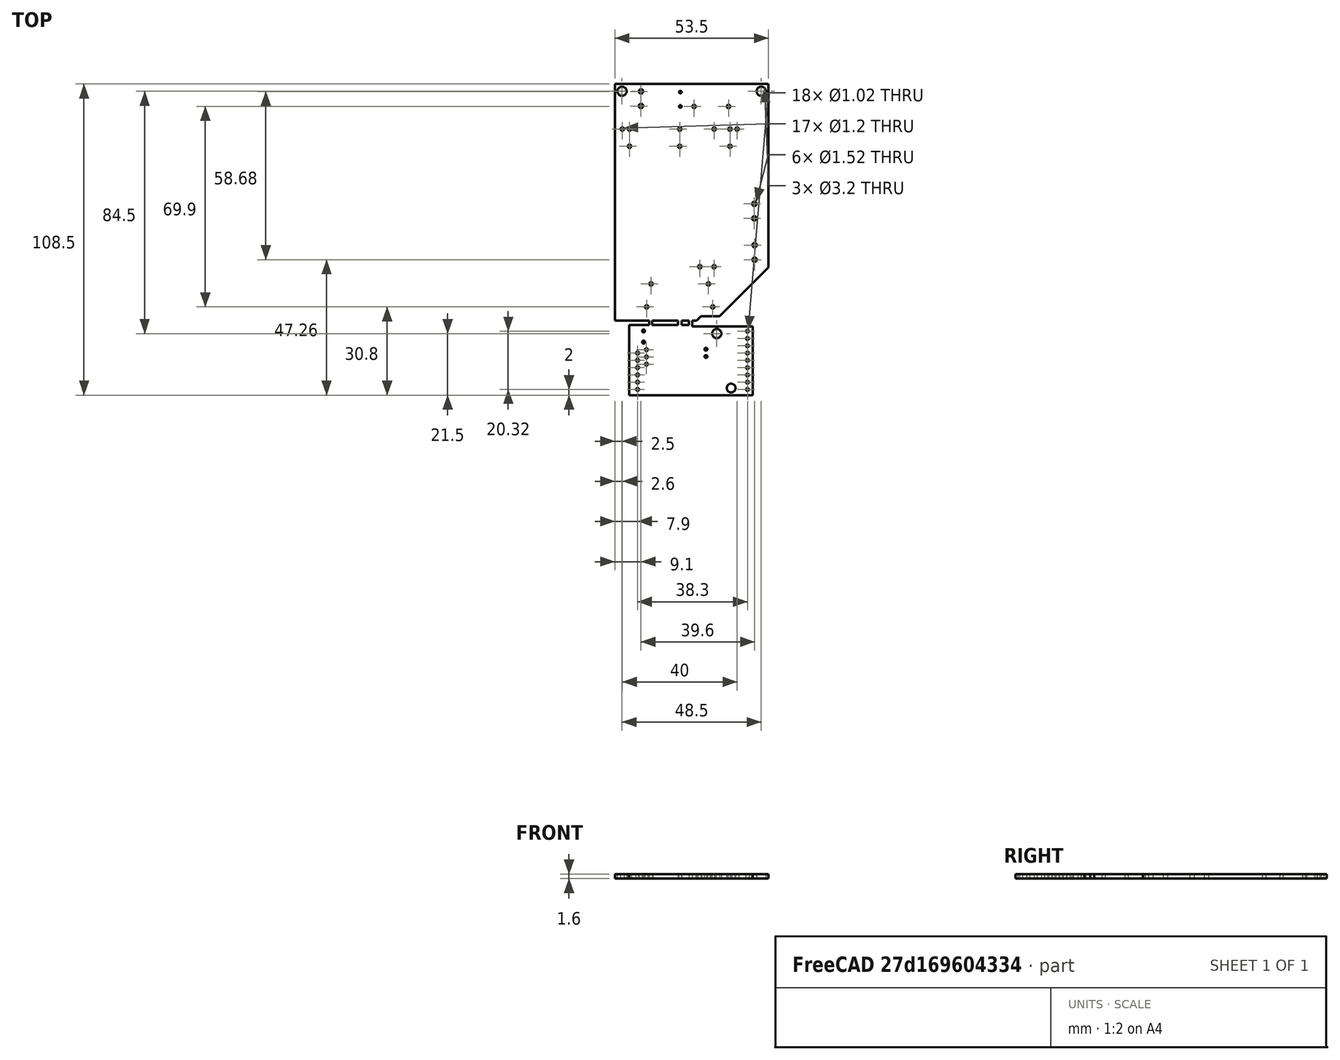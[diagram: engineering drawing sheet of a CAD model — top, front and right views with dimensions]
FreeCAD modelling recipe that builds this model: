
FCSTD DOCUMENT  (FreeCAD 0.16R)
Label: button1
License: All rights reserved
LicenseURL: http://en.wikipedia.org/wiki/All_rights_reserved
objects: App::DocumentObjectGroup×2, Part::Feature×1, Sketcher::SketchObject×1
note: 2 computed .brp shape members not serialized (recipe doc carries the construction recipe); baked Part::Feature solids carry a one-line shape summary decoded from their .brp

FEATURE [Part::Feature] Pcb
  Placement = pos=(-71.75,-78.75,0) rot=(0,0,1;0rad)
  shape: bbox 53.51 x 108.5 x 1.61 mm, 79 faces (baked)
FEATURE [Sketcher::SketchObject] PCB_Sketch
  sketch-geometry (26):
    g0: LineSegment StartX=0.25 StartY=-30.25 StartZ=0 EndX=0.75 EndY=-30.25 EndZ=0
    g1: LineSegment StartX=0.75 StartY=-28.25 StartZ=0 EndX=0.25 EndY=-28.25 EndZ=0
    g2: LineSegment StartX=0.25 StartY=-28.25 StartZ=0 EndX=0.25 EndY=-30.25 EndZ=0
    g3: LineSegment StartX=-21.75 StartY=-29.75 StartZ=0 EndX=-21.75 EndY=-30.25 EndZ=0
    g4: LineSegment StartX=-14.75 StartY=-29.75 StartZ=0 EndX=-21.75 EndY=-29.75 EndZ=0
    g5: LineSegment StartX=-14.75 StartY=-28.25 StartZ=0 EndX=-14.75 EndY=-29.75 EndZ=0
    g6: LineSegment StartX=-13.75 StartY=-29.75 StartZ=0 EndX=-13.75 EndY=-28.25 EndZ=0
    g7: LineSegment StartX=-4.75 StartY=-29.75 StartZ=0 EndX=-13.75 EndY=-29.75 EndZ=0
    g8: LineSegment StartX=-4.75 StartY=-29.75 StartZ=0 EndX=-4.75 EndY=-28.25 EndZ=0
    g9: LineSegment StartX=-4.75 StartY=-28.25 StartZ=0 EndX=-13.75 EndY=-28.25 EndZ=0
    g10: LineSegment StartX=-1 StartY=-29.75 StartZ=0 EndX=-1 EndY=-28.25 EndZ=0
    g11: LineSegment StartX=-3.5 StartY=-29.75 StartZ=0 EndX=-1 EndY=-29.75 EndZ=0
    g12: LineSegment StartX=-3.5 StartY=-28.25 StartZ=0 EndX=-3.5 EndY=-29.75 EndZ=0
    g13: LineSegment StartX=-1 StartY=-28.25 StartZ=0 EndX=-3.5 EndY=-28.25 EndZ=0
    g14: LineSegment StartX=-26.75 StartY=-28.25 StartZ=0 EndX=-14.75 EndY=-28.25 EndZ=0
    g15: LineSegment StartX=-26.75 StartY=54.25 StartZ=0 EndX=-26.75 EndY=-28.25 EndZ=0
    g16: LineSegment StartX=26.75 StartY=54.25 StartZ=0 EndX=-26.75 EndY=54.25 EndZ=0
    g17: LineSegment StartX=26.75 StartY=-9.75 StartZ=0 EndX=26.75 EndY=54.25 EndZ=0
    g18: LineSegment StartX=9.75 StartY=-26.75 StartZ=0 EndX=26.75 EndY=-9.75 EndZ=0
    g19: LineSegment StartX=3.25 StartY=-26.75 StartZ=0 EndX=9.75 EndY=-26.75 EndZ=0
    g20: LineSegment StartX=1.75 StartY=-28.25 StartZ=0 EndX=3.25 EndY=-26.75 EndZ=0
    g21: LineSegment StartX=0.75 StartY=-28.25 StartZ=0 EndX=1.75 EndY=-28.25 EndZ=0
    g22: LineSegment StartX=21.25 StartY=-30.25 StartZ=0 EndX=0.75 EndY=-30.25 EndZ=0
    g23: LineSegment StartX=21.25 StartY=-54.25 StartZ=0 EndX=21.25 EndY=-30.25 EndZ=0
    g24: LineSegment StartX=-21.75 StartY=-54.25 StartZ=0 EndX=21.25 EndY=-54.25 EndZ=0
    g25: LineSegment StartX=-21.75 StartY=-30.25 StartZ=0 EndX=-21.75 EndY=-54.25 EndZ=0
  constraints (50):
    c: Horizontal(g0)
    c: Coincident(g0,g2)
    c: Coincident(g0,g22)
    c: Horizontal(g1)
    c: Coincident(g1,g2)
    c: Coincident(g1,g21)
    c: Vertical(g2)
    c: Vertical(g3)
    c: Coincident(g3,g4)
    c: Coincident(g3,g25)
    c: Horizontal(g4)
    c: Coincident(g4,g5)
    c: Vertical(g5)
    c: Coincident(g5,g14)
    c: Vertical(g6)
    c: Coincident(g6,g7)
    c: Coincident(g6,g9)
    c: Horizontal(g7)
    c: Coincident(g7,g8)
    c: Vertical(g8)
    c: Coincident(g8,g9)
    c: Horizontal(g9)
    c: Vertical(g10)
    c: Coincident(g10,g11)
    c: Coincident(g10,g13)
    c: Horizontal(g11)
    c: Coincident(g11,g12)
    c: Vertical(g12)
    c: Coincident(g12,g13)
    c: Horizontal(g13)
    c: Horizontal(g14)
    c: Coincident(g14,g15)
    c: Vertical(g15)
    c: Coincident(g15,g16)
    c: Horizontal(g16)
    c: Coincident(g16,g17)
    c: Vertical(g17)
    c: Coincident(g17,g18)
    c: Coincident(g18,g19)
    c: Horizontal(g19)
    c: Coincident(g19,g20)
    c: Coincident(g20,g21)
    c: Horizontal(g21)
    c: Horizontal(g22)
    c: Coincident(g22,g23)
    c: Vertical(g23)
    c: Coincident(g23,g24)
    c: Horizontal(g24)
    c: Coincident(g24,g25)
    c: Vertical(g25)
FEATURE [App::DocumentObjectGroup] Board_Geoms
  Group = -> [Pcb,PCB_Sketch]
FEATURE [App::DocumentObjectGroup] Step_Models
